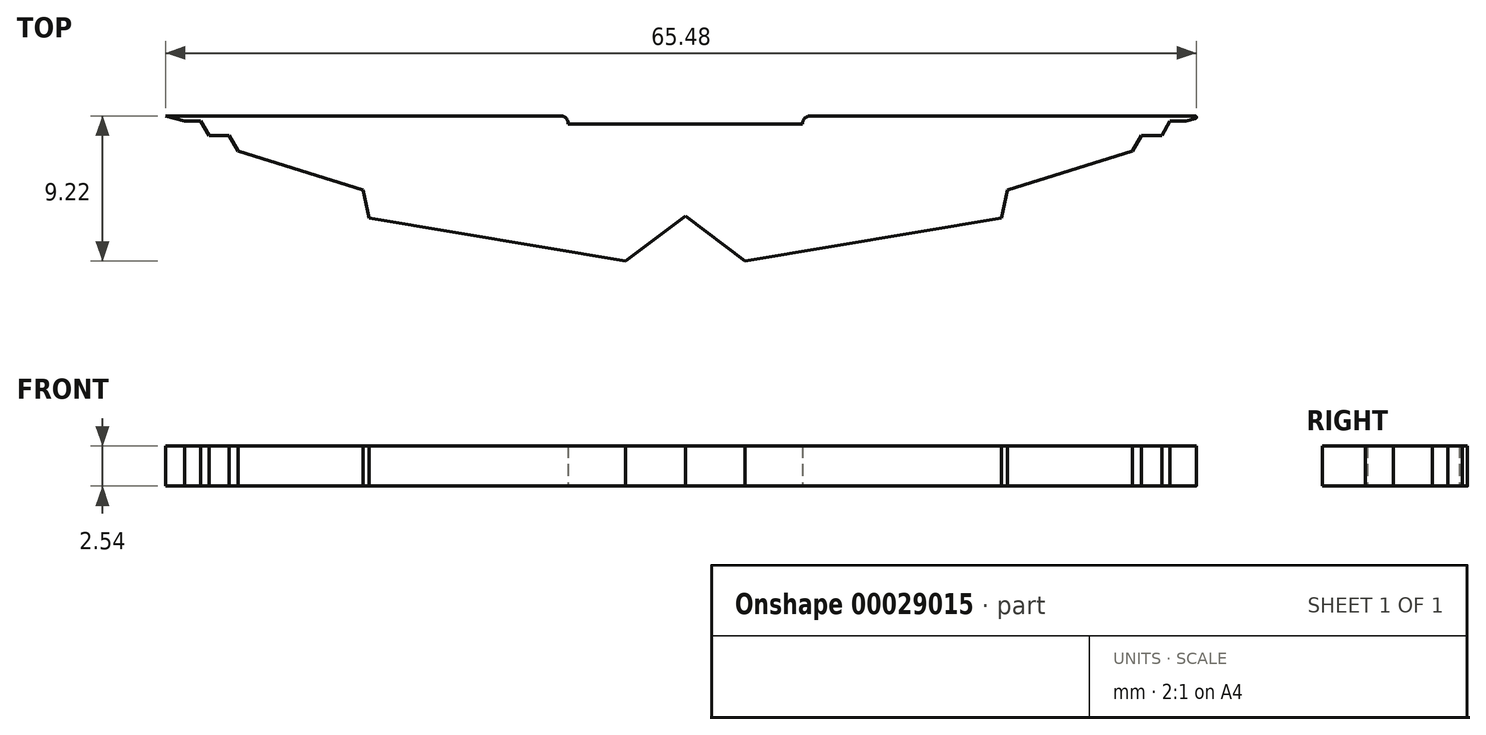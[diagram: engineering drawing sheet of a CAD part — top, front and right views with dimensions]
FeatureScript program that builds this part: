
annotation { "Feature Type Name" : "Feature", "Feature Type Description" : "" }
export const myFeature = defineFeature(function(context is Context, id is Id, definition is map)
    precondition{}
    {
        {
            var Q0;
            Q0=qCreatedBy(makeId("Top.planeOp"),FACE);
            var sketch = newSketch(context, id + "F0", { "sketchPlane" : qUnion([Q0])});
            skPoint(sketch, "E0.rect.middle", {"position": v(0, 9.53) * mm});
            skLineSegment(sketch, "E1", {"start": v(7.44, 28.46) * mm, "end": v(7.44, 28.46) * mm});
            skLineSegment(sketch, "E2", {"start": v(7.94, 28.97) * mm, "end": v(32.37, 28.97) * mm});
            skLineSegment(sketch, "E3", {"start": v(32.4, 28.8) * mm, "end": v(31.8, 28.65) * mm});
            skLineSegment(sketch, "E4", {"start": v(31.78, 28.64) * mm, "end": v(30.78, 28.64) * mm});
            skLineSegment(sketch, "E5", {"start": v(30.78, 28.64) * mm, "end": v(30.26, 27.74) * mm});
            skLineSegment(sketch, "E6", {"start": v(30.26, 27.74) * mm, "end": v(28.98, 27.74) * mm});
            skLineSegment(sketch, "E7", {"start": v(28.98, 27.74) * mm, "end": v(28.4, 26.73) * mm});
            skLineSegment(sketch, "E8", {"start": v(28.4, 26.73) * mm, "end": v(20.47, 24.26) * mm});
            skLineSegment(sketch, "E9", {"start": v(20.47, 24.26) * mm, "end": v(20.07, 22.5) * mm});
            skLineSegment(sketch, "E10", {"start": v(20.07, 22.5) * mm, "end": v(3.8, 19.75) * mm});
            skLineSegment(sketch, "E11", {"start": v(3.8, 19.75) * mm, "end": v(0, 22.61) * mm});
            skPoint(sketch, "E12.visualSharp", {"position": v(7.44, 28.97) * mm});
            skArc(sketch, "E12.filletArc", {"start": v(7.94, 28.97) * mm, "mid": v(7.58, 28.82) * mm, "end": v(7.44, 28.46) * mm});
            skArc(sketch, "E13.MirrorCS", {"start": v(-7.94, 28.97) * mm, "mid": v(-7.58, 28.82) * mm, "end": v(-7.44, 28.46) * mm});
            skLineSegment(sketch, "E14.MirrorCS", {"start": v(-33.02, 28.97) * mm, "end": v(-31.8, 28.64) * mm});
            skLineSegment(sketch, "E15.MirrorCS", {"start": v(-30.78, 28.64) * mm, "end": v(-30.26, 27.74) * mm});
            skLineSegment(sketch, "E16.MirrorCS", {"start": v(-28.98, 27.74) * mm, "end": v(-28.4, 26.73) * mm});
            skLineSegment(sketch, "E17.MirrorCS", {"start": v(-31.8, 28.64) * mm, "end": v(-30.78, 28.64) * mm});
            skLineSegment(sketch, "E18.MirrorCS", {"start": v(-30.26, 27.74) * mm, "end": v(-28.98, 27.74) * mm});
            skLineSegment(sketch, "E19.MirrorCS", {"start": v(-7.44, 28.46) * mm, "end": v(-7.44, 28.46) * mm});
            skPoint(sketch, "E20.MirrorP", {"position": v(-7.44, 28.97) * mm});
            skLineSegment(sketch, "E21.MirrorCS", {"start": v(-7.94, 28.97) * mm, "end": v(-33.02, 28.97) * mm});
            skLineSegment(sketch, "E22.MirrorCS", {"start": v(-20.47, 24.26) * mm, "end": v(-20.07, 22.5) * mm});
            skLineSegment(sketch, "E23.MirrorCS", {"start": v(-20.07, 22.5) * mm, "end": v(-3.8, 19.75) * mm});
            skLineSegment(sketch, "E24.MirrorCS", {"start": v(-28.4, 26.73) * mm, "end": v(-20.47, 24.26) * mm});
            skLineSegment(sketch, "E25", {"start": v(-3.8, 19.75) * mm, "end": v(0, 22.61) * mm});
            skLineSegment(sketch, "E26", {"start": v(-7.44, 28.46) * mm, "end": v(7.44, 28.46) * mm});
            skPoint(sketch, "E27.visualSharp", {"position": v(33.02, 28.97) * mm});
            skArc(sketch, "E27.filletArc", {"start": v(32.4, 28.8) * mm, "mid": v(32.46, 28.9) * mm, "end": v(32.37, 28.97) * mm});
            skPoint(sketch, "E28.visualSharp", {"position": v(31.8, 28.64) * mm});
            skArc(sketch, "E28.filletArc", {"start": v(31.78, 28.64) * mm, "mid": v(31.8, 28.64) * mm, "end": v(31.8, 28.65) * mm});
            skLineSegment(sketch, "E29.rect.bottom", {"start": v(15.1, 28.1) * mm, "end": v(-15.1, 28.1) * mm});
            skLineSegment(sketch, "E29.rect.top", {"start": v(15.1, 24.77) * mm, "end": v(-15.1, 24.77) * mm});
            skLineSegment(sketch, "E29.rect.left", {"start": v(15.1, 28.1) * mm, "end": v(15.1, 24.77) * mm});
            skLineSegment(sketch, "E29.rect.right", {"start": v(-15.1, 28.1) * mm, "end": v(-15.1, 24.77) * mm});
            skPoint(sketch, "E29.rect.middle", {"position": v(0, 26.43) * mm});
            skSolve(sketch);
        }
        {
            var Q0;
            Q0=makeQuery(id+"F0.imprint","IMPRINT",FACE,{"disambiguationData":[TD([[makeQuery(id+"F0.imprint","IMPRINT",EDGE,{"derivedFrom":sQuery(id+"F0.wireOp",EDGE,"E29.rect.bottom")}),1.0]])]});
            extrude(context, id + "F1", {"entities" : qUnion([Q0]), "depth" : 2.54 * mm});
        }
        {
            var Q0;
            Q0 = qSketchRegion(id + "F0", true);
            extrude(context, id + "F2", {"entities" : qUnion([Q0]), "operationType" : NewBodyOperationType.ADD, "depth" : 2.54 * mm});
        }
    });
